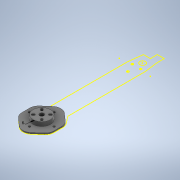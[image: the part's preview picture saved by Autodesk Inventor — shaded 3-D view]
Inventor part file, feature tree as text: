
AUTODESK INVENTOR PART (.ipt)
format: ipt  version: 2020 (Build 240168000, 168)  size: 450,048 bytes
history: native  units: in
note: dims shown in document units (in); Inventor stores cm internally (conversion verified against a paired STEP export)
features: sketch x8, extrude x8, projected_geometry x6, fillet x1
ambient origin geometry x8: Origin, YZ Plane, XZ Plane, XY Plane, X Axis, Y Axis, Z Axis, Center Point
bodies: Solid1 (feature_tree)
feature tree (23):
  sketch  "Sketch1"  dims[d0=0.2362in d1=0.0in d2=0.1181in]
  extrude  "Extrusion1"  Depth=0.1181in
  extrude  "Extrusion2"  Depth=0.3937in
  sketch  "Sketch3"  dims[d9=0.2362in d10=0.0in d11=0.1181in]
  fillet  "Fillet1"  Radius=0.2362in
  extrude  "Extrusion3"  Depth=0.1181in
  extrude  "Extrusion4"  Depth=0.2362in TaperAngle=0.0deg
  extrude  "Extrusion5"  Depth=0.315in TaperAngle=0.0deg
  extrude  "Extrusion6"  Depth=0.315in TaperAngle=0.0deg
  extrude  "Extrusion7"  [1 undecoded]
  sketch  "Sketch7"
  extrude  "Extrusion8"  [1 undecoded]
  sketch  "Sketch2"  dims[d3=0.2362in d4=0.0in d7=0.3937in d8=0.2362in]
  projected_geometry  "Projected Loop1"
  projected_geometry  "Projected Loop2"
  sketch  "Sketch4"  dims[d12=1.5748in d14=360.0deg d16=0.2362in d17=0.0in]
  sketch  "Sketch5"  dims[d18=0.0787in d19=0.0in d20=0.315in d21=0.0in]
  projected_geometry  "Projected Loop3"
  sketch  "Sketch6"  dims[d22=0.2362in d23=0.0in d24=0.315in d25=0.0in]
  projected_geometry  "Projected Loop4"
  sketch  "Sketch8"
  projected_geometry  "Projected Loop5"
  projected_geometry  "Projected Loop6"
note: 2 required parameter values undecoded (feature->parameter linkage not recoverable at this tier; creation-order binding heuristic only, values carry confidence <= 0.55)
